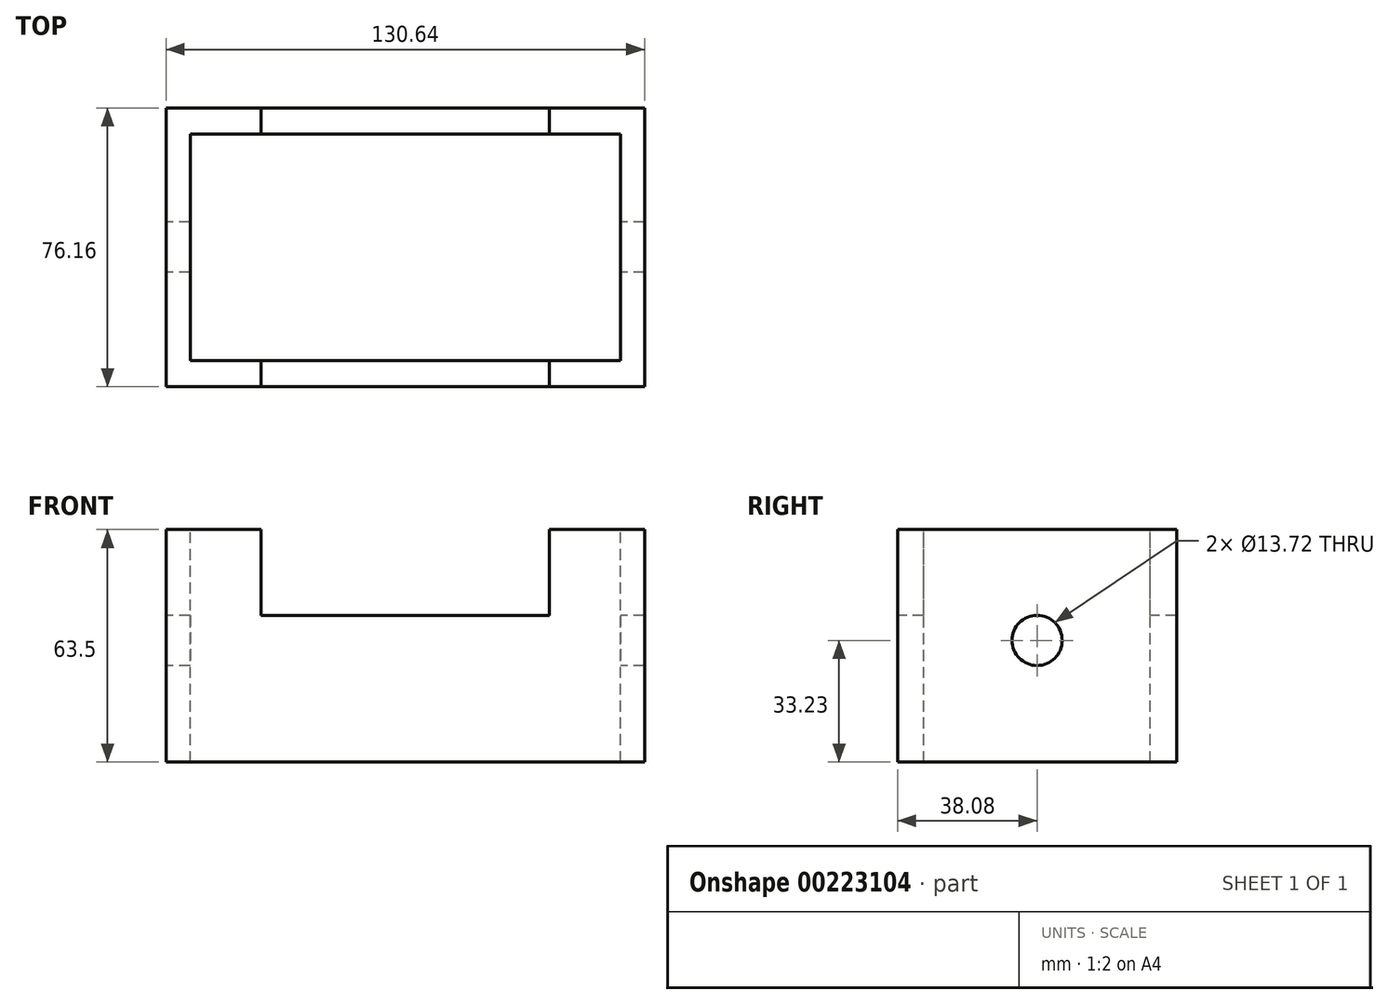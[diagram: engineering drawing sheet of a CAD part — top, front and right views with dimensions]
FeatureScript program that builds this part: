
annotation { "Feature Type Name" : "Feature", "Feature Type Description" : "" }
export const myFeature = defineFeature(function(context is Context, id is Id, definition is map)
    precondition{}
    {
        {
            var Q0;
            Q0=qCreatedBy(makeId("Top.planeOp"),FACE);
            var sketch = newSketch(context, id + "F0", { "sketchPlane" : qUnion([Q0])});
            skLineSegment(sketch, "E0.bottom", {"start": v(65.32, 38.08) * mm, "end": v(-65.32, 38.08) * mm});
            skLineSegment(sketch, "E0.top", {"start": v(65.32, -38.08) * mm, "end": v(-65.32, -38.08) * mm});
            skLineSegment(sketch, "E0.left", {"start": v(65.32, 38.08) * mm, "end": v(65.32, -38.08) * mm});
            skLineSegment(sketch, "E0.right", {"start": v(-65.32, 38.08) * mm, "end": v(-65.32, -38.08) * mm});
            skPoint(sketch, "E0.middle", {"position": v(0, 0) * mm});
            skSolve(sketch);
        }
        {
            var Q0;
            Q0=makeQuery(id+"F0.imprint","IMPRINT",FACE,{"disambiguationData":[TD([[makeQuery(id+"F0.imprint","IMPRINT",EDGE,{"derivedFrom":sQuery(id+"F0.wireOp",EDGE,"E0.bottom")}),1.0]])]});
            extrude(context, id + "F1", {"entities" : qUnion([Q0]), "depth" : 63.5 * mm});
        }
        {
            var Q0;
            Q0=makeQuery(id+"F1.opExtrude","CAP_FACE",FACE,{"disambiguationData":[OSD([sQuery(id+"F0.wireOp",EDGE,"E0.bottom"),sQuery(id+"F0.wireOp",EDGE,"E0.top"),sQuery(id+"F0.wireOp",EDGE,"E0.left"),sQuery(id+"F0.wireOp",EDGE,"E0.right")])],"isStart":false});
            var sketch = newSketch(context, id + "F2", { "sketchPlane" : qUnion([Q0])});
            skLineSegment(sketch, "E1.bottom", {"start": v(58.76, 30.95) * mm, "end": v(-58.76, 30.95) * mm});
            skLineSegment(sketch, "E1.top", {"start": v(58.76, -30.95) * mm, "end": v(-58.76, -30.95) * mm});
            skLineSegment(sketch, "E1.left", {"start": v(58.76, 30.95) * mm, "end": v(58.76, -30.95) * mm});
            skLineSegment(sketch, "E1.right", {"start": v(-58.76, 30.95) * mm, "end": v(-58.76, -30.95) * mm});
            skPoint(sketch, "E1.middle", {"position": v(0, 0) * mm});
            skSolve(sketch);
        }
        {
            var Q0;
            Q0 = qSketchRegion(id + "F2", true);
            extrude(context, id + "F3", {"entities" : qUnion([Q0]), "operationType" : NewBodyOperationType.REMOVE, "oppositeDirection" : true, "depth" : 63.5 * mm});
        }
        {
            var Q0;
            Q0=makeQuery(id+"F1.opExtrude","SWEPT_FACE",FACE,{"disambiguationData":[OSD([sQuery(id+"F0.wireOp",EDGE,"E0.top")])]});
            var sketch = newSketch(context, id + "F4", { "sketchPlane" : qUnion([Q0])});
            skLineSegment(sketch, "E2.bottom", {"start": v(39.39, 63.5) * mm, "end": v(-39.39, 63.5) * mm});
            skLineSegment(sketch, "E2.top", {"start": v(39.39, 40.04) * mm, "end": v(-39.39, 40.04) * mm});
            skLineSegment(sketch, "E2.left", {"start": v(39.39, 63.5) * mm, "end": v(39.39, 40.04) * mm});
            skLineSegment(sketch, "E2.right", {"start": v(-39.39, 63.5) * mm, "end": v(-39.39, 40.04) * mm});
            skPoint(sketch, "E2.middle", {"position": v(0, 51.77) * mm});
            skSolve(sketch);
        }
        {
            var Q0;
            Q0 = qSketchRegion(id + "F4", true);
            extrude(context, id + "F5", {"entities" : qUnion([Q0]), "operationType" : NewBodyOperationType.REMOVE, "oppositeDirection" : true, "depth" : 101.6 * mm});
        }
        {
            var Q0;
            Q0=makeQuery(id+"F1.opExtrude","SWEPT_FACE",FACE,{"disambiguationData":[OSD([sQuery(id+"F0.wireOp",EDGE,"E0.right")])]});
            var sketch = newSketch(context, id + "F6", { "sketchPlane" : qUnion([Q0])});
            skCircle(sketch, "E3", {"center": v(0, 33.23) * mm, "radius": 6.86 * mm});
            skSolve(sketch);
        }
        {
            var Q0;
            Q0 = qSketchRegion(id + "F6", true);
            extrude(context, id + "F7", {"entities" : qUnion([Q0]), "operationType" : NewBodyOperationType.REMOVE, "oppositeDirection" : true, "depth" : 152.4 * mm});
        }
    });
